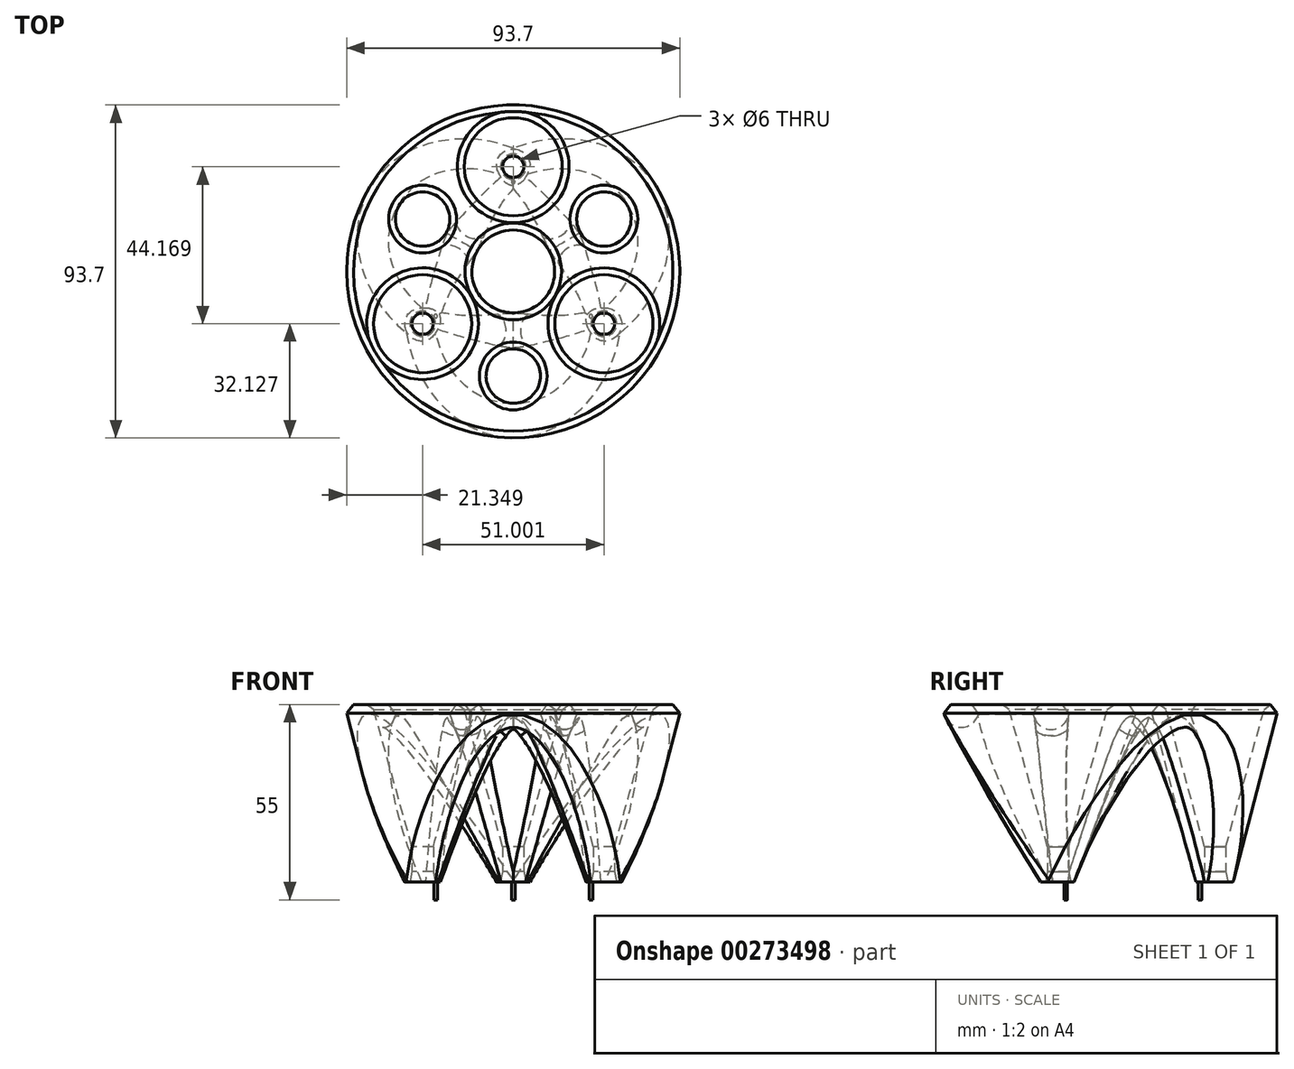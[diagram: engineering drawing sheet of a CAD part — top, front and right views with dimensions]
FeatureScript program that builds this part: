
annotation { "Feature Type Name" : "Feature", "Feature Type Description" : "" }
export const myFeature = defineFeature(function(context is Context, id is Id, definition is map)
    precondition{}
    {
        {
            var Q0;
            Q0=qCreatedBy(makeId("Top.planeOp"),FACE);
            var sketch = newSketch(context, id + "F0", { "sketchPlane" : qUnion([Q0])});
            skCircle(sketch, "E0", {"center": v(0, 0) * mm, "radius": 47.5 * mm});
            skCircle(sketch, "E1", {"center": v(0, 0) * mm, "radius": 11 * mm});
            skCircle(sketch, "E2", {"center": v(0, 29.45) * mm, "radius": 3 * mm});
            skCircle(sketch, "E3.1.0", {"center": v(-25.5, 14.72) * mm, "radius": 3 * mm});
            skCircle(sketch, "E3.2.0", {"center": v(-25.5, -14.72) * mm, "radius": 3 * mm});
            skCircle(sketch, "E4.1.3.0", {"center": v(0, -29.45) * mm, "radius": 3 * mm});
            skCircle(sketch, "E4.1.4.0", {"center": v(25.5, -14.72) * mm, "radius": 3 * mm});
            skCircle(sketch, "E4.1.5.0", {"center": v(25.5, 14.72) * mm, "radius": 3 * mm});
            skCircle(sketch, "E5", {"center": v(0, 25.2) * mm, "radius": 0.5 * mm});
            skCircle(sketch, "E6.1.0", {"center": v(-21.83, -12.6) * mm, "radius": 0.5 * mm});
            skCircle(sketch, "E6.2.0", {"center": v(21.83, -12.6) * mm, "radius": 0.5 * mm});
            skSolve(sketch);
        }
        {
            var Q0;
            Q0=makeQuery(id+"F0.imprint","IMPRINT",FACE,{"disambiguationData":[TD([[makeQuery(id+"F0.imprint","IMPRINT",EDGE,{"derivedFrom":sQuery(id+"F0.wireOp",EDGE,"E0")}),1.0]])]});
            var Q1;
            Q1=makeQuery(id+"F0.imprint","IMPRINT",FACE,{"disambiguationData":[TD([[makeQuery(id+"F0.imprint","IMPRINT",EDGE,{"derivedFrom":sQuery(id+"F0.wireOp",EDGE,"E6.1.0")}),1.0]])]});
            var Q2;
            Q2=makeQuery(id+"F0.imprint","IMPRINT",FACE,{"disambiguationData":[TD([[makeQuery(id+"F0.imprint","IMPRINT",EDGE,{"derivedFrom":sQuery(id+"F0.wireOp",EDGE,"E6.2.0")}),1.0]])]});
            var Q3;
            Q3=makeQuery(id+"F0.imprint","IMPRINT",FACE,{"disambiguationData":[TD([[makeQuery(id+"F0.imprint","IMPRINT",EDGE,{"derivedFrom":sQuery(id+"F0.wireOp",EDGE,"E5")}),1.0]])]});
            extrude(context, id + "F1", {"entities" : qUnion([Q0, Q1, Q2, Q3]), "depth" : 50 * mm});
        }
        {
            var Q0;
            Q0=makeQuery(id+"F0.imprint","IMPRINT",FACE,{"disambiguationData":[TD([[makeQuery(id+"F0.imprint","IMPRINT",EDGE,{"derivedFrom":sQuery(id+"F0.wireOp",EDGE,"E5")}),1.0]])]});
            var Q1;
            Q1=makeQuery(id+"F0.imprint","IMPRINT",FACE,{"disambiguationData":[TD([[makeQuery(id+"F0.imprint","IMPRINT",EDGE,{"derivedFrom":sQuery(id+"F0.wireOp",EDGE,"E6.1.0")}),1.0]])]});
            var Q2;
            Q2=makeQuery(id+"F0.imprint","IMPRINT",FACE,{"disambiguationData":[TD([[makeQuery(id+"F0.imprint","IMPRINT",EDGE,{"derivedFrom":sQuery(id+"F0.wireOp",EDGE,"E6.2.0")}),1.0]])]});
            extrude(context, id + "F2", {"entities" : qUnion([Q0, Q1, Q2]), "operationType" : NewBodyOperationType.ADD, "depth" : 10 * mm, "symmetric" : true});
        }
        {
            var Q0;
            Q0=makeQuery(id+"F1.opExtrude","CAP_EDGE",EDGE,{"disambiguationData":[OSD([sQuery(id+"F0.wireOp",EDGE,"E2")])],"isStart":false});
            var Q1;
            Q1=makeQuery(id+"F1.opExtrude","CAP_EDGE",EDGE,{"disambiguationData":[OSD([sQuery(id+"F0.wireOp",EDGE,"E4.1.4.0")])],"isStart":false});
            var Q2;
            Q2=makeQuery(id+"F1.opExtrude","CAP_EDGE",EDGE,{"disambiguationData":[OSD([sQuery(id+"F0.wireOp",EDGE,"E3.2.0")])],"isStart":false});
            chamfer(context, id + "F3", {"entities" : qUnion([Q0, Q1, Q2]), "chamferType" : ChamferType.TWO_OFFSETS, "width1" : 40 * mm, "oppositeDirection" : false, "width2" : 11.2 * mm, "tangentPropagation" : true});
        }
        {
            var Q0;
            Q0=makeQuery(id+"F1.opExtrude","CAP_EDGE",EDGE,{"disambiguationData":[OSD([sQuery(id+"F0.wireOp",EDGE,"E0")])],"isStart":true});
            chamfer(context, id + "F4", {"entities" : qUnion([Q0]), "chamferType" : ChamferType.TWO_OFFSETS, "width1" : 50 * mm, "oppositeDirection" : false, "width2" : 13 * mm, "tangentPropagation" : true});
        }
        {
            var Q0;
            Q0=makeQuery(id+"F1.opExtrude","CAP_EDGE",EDGE,{"disambiguationData":[OSD([sQuery(id+"F0.wireOp",EDGE,"E2")])],"isStart":true});
            var Q1;
            Q1=makeQuery(id+"F1.opExtrude","CAP_EDGE",EDGE,{"disambiguationData":[OSD([sQuery(id+"F0.wireOp",EDGE,"E3.2.0")])],"isStart":true});
            var Q2;
            Q2=makeQuery(id+"F1.opExtrude","CAP_EDGE",EDGE,{"disambiguationData":[OSD([sQuery(id+"F0.wireOp",EDGE,"E4.1.4.0")])],"isStart":true});
            chamfer(context, id + "F5", {"entities" : qUnion([Q0, Q1, Q2]), "chamferType" : ChamferType.TWO_OFFSETS, "width1" : 0.6 * mm, "oppositeDirection" : false, "width2" : 3 * mm, "tangentPropagation" : true});
        }
        {
            var Q0;
            Q0=makeQuery(id+"F1.opExtrude","CAP_EDGE",EDGE,{"disambiguationData":[OSD([sQuery(id+"F0.wireOp",EDGE,"E1")])],"isStart":true});
            chamfer(context, id + "F6", {"entities" : qUnion([Q0]), "chamferType" : ChamferType.TWO_OFFSETS, "width1" : 13 * mm, "oppositeDirection" : false, "width2" : 50 * mm, "tangentPropagation" : true});
        }
        {
            var Q0;
            Q0=makeQuery(id+"F1.opExtrude","CAP_EDGE",EDGE,{"disambiguationData":[OSD([sQuery(id+"F0.wireOp",EDGE,"E4.1.5.0")])],"isStart":true});
            var Q1;
            Q1=makeQuery(id+"F1.opExtrude","CAP_EDGE",EDGE,{"disambiguationData":[OSD([sQuery(id+"F0.wireOp",EDGE,"E4.1.3.0")])],"isStart":true});
            var Q2;
            Q2=makeQuery(id+"F1.opExtrude","CAP_EDGE",EDGE,{"disambiguationData":[OSD([sQuery(id+"F0.wireOp",EDGE,"E3.1.0")])],"isStart":true});
            chamfer(context, id + "F7", {"entities" : qUnion([Q0, Q1, Q2]), "chamferType" : ChamferType.TWO_OFFSETS, "width1" : 22 * mm, "oppositeDirection" : false, "width2" : 60 * mm, "tangentPropagation" : true});
        }
        {
            var Q0;
            {var subQ0=sQuery(id+"F0.wireOp",EDGE,"E0");Q0=makeQuery(id+"F4.opChamfer","BLEND_EDGE",EDGE,{"blendedFrom":[makeQuery(id+"F1.opExtrude","CAP_EDGE",EDGE,{"disambiguationData":[OSD([subQ0])],"isStart":true}),makeQuery(id+"F1.opExtrude","CAP_FACE",FACE,{"disambiguationData":[OSD([subQ0,sQuery(id+"F0.wireOp",EDGE,"E1"),sQuery(id+"F0.wireOp",EDGE,"E2"),sQuery(id+"F0.wireOp",EDGE,"E3.1.0"),sQuery(id+"F0.wireOp",EDGE,"E3.2.0")])],"isStart":false})],"blendedInto":[makeQuery(id+"F1.opExtrude","CAP_FACE",FACE,{"disambiguationData":[OSD([subQ0,sQuery(id+"F0.wireOp",EDGE,"E1"),sQuery(id+"F0.wireOp",EDGE,"E2"),sQuery(id+"F0.wireOp",EDGE,"E3.1.0"),sQuery(id+"F0.wireOp",EDGE,"E3.2.0")])],"isStart":false})]});}
            var Q1;
            {var subQ0=sQuery(id+"F0.wireOp",EDGE,"E1");Q1=makeQuery(id+"F6.opChamfer","BLEND_EDGE",EDGE,{"blendedFrom":[makeQuery(id+"F1.opExtrude","CAP_EDGE",EDGE,{"disambiguationData":[OSD([subQ0])],"isStart":true}),makeQuery(id+"F1.opExtrude","CAP_FACE",FACE,{"disambiguationData":[OSD([sQuery(id+"F0.wireOp",EDGE,"E0"),subQ0,sQuery(id+"F0.wireOp",EDGE,"E2"),sQuery(id+"F0.wireOp",EDGE,"E3.1.0"),sQuery(id+"F0.wireOp",EDGE,"E3.2.0")])],"isStart":false})],"blendedInto":[makeQuery(id+"F1.opExtrude","CAP_FACE",FACE,{"disambiguationData":[OSD([sQuery(id+"F0.wireOp",EDGE,"E0"),subQ0,sQuery(id+"F0.wireOp",EDGE,"E2"),sQuery(id+"F0.wireOp",EDGE,"E3.1.0"),sQuery(id+"F0.wireOp",EDGE,"E3.2.0")])],"isStart":false})]});}
            var Q2;
            {var subQ0=sQuery(id+"F0.wireOp",EDGE,"E3.2.0");Q2=makeQuery(id+"F3.opChamfer","BLEND_EDGE",EDGE,{"blendedFrom":[makeQuery(id+"F1.opExtrude","CAP_EDGE",EDGE,{"disambiguationData":[OSD([subQ0])],"isStart":false}),makeQuery(id+"F1.opExtrude","CAP_FACE",FACE,{"disambiguationData":[OSD([sQuery(id+"F0.wireOp",EDGE,"E0"),sQuery(id+"F0.wireOp",EDGE,"E1"),sQuery(id+"F0.wireOp",EDGE,"E2"),sQuery(id+"F0.wireOp",EDGE,"E3.1.0"),subQ0,sQuery(id+"F0.wireOp",EDGE,"E4.1.3.0"),sQuery(id+"F0.wireOp",EDGE,"E4.1.4.0"),sQuery(id+"F0.wireOp",EDGE,"E4.1.5.0")])],"isStart":false})],"blendedInto":[makeQuery(id+"F1.opExtrude","CAP_FACE",FACE,{"disambiguationData":[OSD([sQuery(id+"F0.wireOp",EDGE,"E0"),sQuery(id+"F0.wireOp",EDGE,"E1"),sQuery(id+"F0.wireOp",EDGE,"E2"),sQuery(id+"F0.wireOp",EDGE,"E3.1.0"),subQ0,sQuery(id+"F0.wireOp",EDGE,"E4.1.3.0"),sQuery(id+"F0.wireOp",EDGE,"E4.1.4.0"),sQuery(id+"F0.wireOp",EDGE,"E4.1.5.0")])],"isStart":false})]});}
            var Q3;
            {var subQ0=sQuery(id+"F0.wireOp",EDGE,"E2");Q3=makeQuery(id+"F3.opChamfer","BLEND_EDGE",EDGE,{"blendedFrom":[makeQuery(id+"F1.opExtrude","CAP_EDGE",EDGE,{"disambiguationData":[OSD([subQ0])],"isStart":false}),makeQuery(id+"F1.opExtrude","CAP_FACE",FACE,{"disambiguationData":[OSD([sQuery(id+"F0.wireOp",EDGE,"E0"),sQuery(id+"F0.wireOp",EDGE,"E1"),subQ0,sQuery(id+"F0.wireOp",EDGE,"E3.1.0"),sQuery(id+"F0.wireOp",EDGE,"E3.2.0"),sQuery(id+"F0.wireOp",EDGE,"E4.1.3.0"),sQuery(id+"F0.wireOp",EDGE,"E4.1.4.0"),sQuery(id+"F0.wireOp",EDGE,"E4.1.5.0")])],"isStart":false})],"blendedInto":[makeQuery(id+"F1.opExtrude","CAP_FACE",FACE,{"disambiguationData":[OSD([sQuery(id+"F0.wireOp",EDGE,"E0"),sQuery(id+"F0.wireOp",EDGE,"E1"),subQ0,sQuery(id+"F0.wireOp",EDGE,"E3.1.0"),sQuery(id+"F0.wireOp",EDGE,"E3.2.0"),sQuery(id+"F0.wireOp",EDGE,"E4.1.3.0"),sQuery(id+"F0.wireOp",EDGE,"E4.1.4.0"),sQuery(id+"F0.wireOp",EDGE,"E4.1.5.0")])],"isStart":false})]});}
            var Q4;
            {var subQ0=sQuery(id+"F0.wireOp",EDGE,"E4.1.4.0");Q4=makeQuery(id+"F3.opChamfer","BLEND_EDGE",EDGE,{"blendedFrom":[makeQuery(id+"F1.opExtrude","CAP_EDGE",EDGE,{"disambiguationData":[OSD([subQ0])],"isStart":false}),makeQuery(id+"F1.opExtrude","CAP_FACE",FACE,{"disambiguationData":[OSD([sQuery(id+"F0.wireOp",EDGE,"E0"),sQuery(id+"F0.wireOp",EDGE,"E1"),sQuery(id+"F0.wireOp",EDGE,"E2"),sQuery(id+"F0.wireOp",EDGE,"E3.1.0"),sQuery(id+"F0.wireOp",EDGE,"E3.2.0"),sQuery(id+"F0.wireOp",EDGE,"E4.1.3.0"),subQ0,sQuery(id+"F0.wireOp",EDGE,"E4.1.5.0")])],"isStart":false})],"blendedInto":[makeQuery(id+"F1.opExtrude","CAP_FACE",FACE,{"disambiguationData":[OSD([sQuery(id+"F0.wireOp",EDGE,"E0"),sQuery(id+"F0.wireOp",EDGE,"E1"),sQuery(id+"F0.wireOp",EDGE,"E2"),sQuery(id+"F0.wireOp",EDGE,"E3.1.0"),sQuery(id+"F0.wireOp",EDGE,"E3.2.0"),sQuery(id+"F0.wireOp",EDGE,"E4.1.3.0"),subQ0,sQuery(id+"F0.wireOp",EDGE,"E4.1.5.0")])],"isStart":false})]});}
            var Q5;
            Q5=makeQuery(id+"F1.opExtrude","CAP_EDGE",EDGE,{"disambiguationData":[OSD([sQuery(id+"F0.wireOp",EDGE,"E4.1.3.0")])],"isStart":false});
            var Q6;
            Q6=makeQuery(id+"F1.opExtrude","CAP_EDGE",EDGE,{"disambiguationData":[OSD([sQuery(id+"F0.wireOp",EDGE,"E3.1.0")])],"isStart":false});
            var Q7;
            Q7=makeQuery(id+"F1.opExtrude","CAP_EDGE",EDGE,{"disambiguationData":[OSD([sQuery(id+"F0.wireOp",EDGE,"E4.1.5.0")])],"isStart":false});
            var Q8;
            {var subQ0=sQuery(id+"F0.wireOp",EDGE,"E3.1.0");Q8=makeQuery(id+"F7.opChamfer","BLEND_EDGE",EDGE,{"blendedFrom":[makeQuery(id+"F1.opExtrude","CAP_EDGE",EDGE,{"disambiguationData":[OSD([subQ0])],"isStart":true}),makeQuery(id+"F1.opExtrude","CAP_FACE",FACE,{"disambiguationData":[OSD([sQuery(id+"F0.wireOp",EDGE,"E0"),sQuery(id+"F0.wireOp",EDGE,"E1"),sQuery(id+"F0.wireOp",EDGE,"E2"),subQ0,sQuery(id+"F0.wireOp",EDGE,"E3.2.0"),sQuery(id+"F0.wireOp",EDGE,"E4.1.3.0"),sQuery(id+"F0.wireOp",EDGE,"E4.1.4.0"),sQuery(id+"F0.wireOp",EDGE,"E4.1.5.0")])],"isStart":false})],"blendedInto":[makeQuery(id+"F1.opExtrude","CAP_FACE",FACE,{"disambiguationData":[OSD([sQuery(id+"F0.wireOp",EDGE,"E0"),sQuery(id+"F0.wireOp",EDGE,"E1"),sQuery(id+"F0.wireOp",EDGE,"E2"),subQ0,sQuery(id+"F0.wireOp",EDGE,"E3.2.0"),sQuery(id+"F0.wireOp",EDGE,"E4.1.3.0"),sQuery(id+"F0.wireOp",EDGE,"E4.1.4.0"),sQuery(id+"F0.wireOp",EDGE,"E4.1.5.0")])],"isStart":false})]});}
            var Q9;
            {var subQ0=sQuery(id+"F0.wireOp",EDGE,"E4.1.3.0");Q9=makeQuery(id+"F7.opChamfer","BLEND_EDGE",EDGE,{"blendedFrom":[makeQuery(id+"F1.opExtrude","CAP_EDGE",EDGE,{"disambiguationData":[OSD([subQ0])],"isStart":true}),makeQuery(id+"F1.opExtrude","CAP_FACE",FACE,{"disambiguationData":[OSD([sQuery(id+"F0.wireOp",EDGE,"E0"),sQuery(id+"F0.wireOp",EDGE,"E1"),sQuery(id+"F0.wireOp",EDGE,"E2"),sQuery(id+"F0.wireOp",EDGE,"E3.1.0"),sQuery(id+"F0.wireOp",EDGE,"E3.2.0"),subQ0,sQuery(id+"F0.wireOp",EDGE,"E4.1.4.0"),sQuery(id+"F0.wireOp",EDGE,"E4.1.5.0")])],"isStart":false})],"blendedInto":[makeQuery(id+"F1.opExtrude","CAP_FACE",FACE,{"disambiguationData":[OSD([sQuery(id+"F0.wireOp",EDGE,"E0"),sQuery(id+"F0.wireOp",EDGE,"E1"),sQuery(id+"F0.wireOp",EDGE,"E2"),sQuery(id+"F0.wireOp",EDGE,"E3.1.0"),sQuery(id+"F0.wireOp",EDGE,"E3.2.0"),subQ0,sQuery(id+"F0.wireOp",EDGE,"E4.1.4.0"),sQuery(id+"F0.wireOp",EDGE,"E4.1.5.0")])],"isStart":false})]});}
            var Q10;
            {var subQ0=sQuery(id+"F0.wireOp",EDGE,"E4.1.5.0");Q10=makeQuery(id+"F7.opChamfer","BLEND_EDGE",EDGE,{"blendedFrom":[makeQuery(id+"F1.opExtrude","CAP_EDGE",EDGE,{"disambiguationData":[OSD([subQ0])],"isStart":true}),makeQuery(id+"F1.opExtrude","CAP_FACE",FACE,{"disambiguationData":[OSD([sQuery(id+"F0.wireOp",EDGE,"E0"),sQuery(id+"F0.wireOp",EDGE,"E1"),sQuery(id+"F0.wireOp",EDGE,"E2"),sQuery(id+"F0.wireOp",EDGE,"E3.1.0"),sQuery(id+"F0.wireOp",EDGE,"E3.2.0"),sQuery(id+"F0.wireOp",EDGE,"E4.1.3.0"),sQuery(id+"F0.wireOp",EDGE,"E4.1.4.0"),subQ0])],"isStart":false})],"blendedInto":[makeQuery(id+"F1.opExtrude","CAP_FACE",FACE,{"disambiguationData":[OSD([sQuery(id+"F0.wireOp",EDGE,"E0"),sQuery(id+"F0.wireOp",EDGE,"E1"),sQuery(id+"F0.wireOp",EDGE,"E2"),sQuery(id+"F0.wireOp",EDGE,"E3.1.0"),sQuery(id+"F0.wireOp",EDGE,"E3.2.0"),sQuery(id+"F0.wireOp",EDGE,"E4.1.3.0"),sQuery(id+"F0.wireOp",EDGE,"E4.1.4.0"),subQ0])],"isStart":false})]});}
            chamfer(context, id + "F8", {"entities" : qUnion([Q0, Q1, Q2, Q3, Q4, Q5, Q6, Q7, Q8, Q9, Q10]), "width" : 2 * mm, "tangentPropagation" : true});
        }
        {
            var Q0;
            Q0=makeQuery(id+"F7.opChamfer","BLEND_EDGE",EDGE,{"blendedFrom":[makeQuery(id+"F1.opExtrude","CAP_EDGE",EDGE,{"disambiguationData":[OSD([sQuery(id+"F0.wireOp",EDGE,"E4.1.5.0")])],"isStart":true}),makeQuery(id+"F6.opChamfer","BLEND_FACE",FACE,{"disambiguationData":[OSD([sQuery(id+"F0.wireOp",EDGE,"E1")])]})],"blendedInto":[makeQuery(id+"F6.opChamfer","BLEND_FACE",FACE,{"disambiguationData":[OSD([sQuery(id+"F0.wireOp",EDGE,"E1")])]})]});
            var Q1;
            Q1=makeQuery(id+"F7.opChamfer","BLEND_EDGE",EDGE,{"blendedFrom":[makeQuery(id+"F1.opExtrude","CAP_EDGE",EDGE,{"disambiguationData":[OSD([sQuery(id+"F0.wireOp",EDGE,"E3.1.0")])],"isStart":true}),makeQuery(id+"F6.opChamfer","BLEND_FACE",FACE,{"disambiguationData":[OSD([sQuery(id+"F0.wireOp",EDGE,"E1")])]})],"blendedInto":[makeQuery(id+"F6.opChamfer","BLEND_FACE",FACE,{"disambiguationData":[OSD([sQuery(id+"F0.wireOp",EDGE,"E1")])]})]});
            var Q2;
            Q2=makeQuery(id+"F7.opChamfer","BLEND_EDGE",EDGE,{"blendedFrom":[makeQuery(id+"F1.opExtrude","CAP_EDGE",EDGE,{"disambiguationData":[OSD([sQuery(id+"F0.wireOp",EDGE,"E4.1.3.0")])],"isStart":true}),makeQuery(id+"F6.opChamfer","BLEND_FACE",FACE,{"disambiguationData":[OSD([sQuery(id+"F0.wireOp",EDGE,"E1")])]})],"blendedInto":[makeQuery(id+"F6.opChamfer","BLEND_FACE",FACE,{"disambiguationData":[OSD([sQuery(id+"F0.wireOp",EDGE,"E1")])]})]});
            var Q3;
            Q3=makeQuery(id+"F7.opChamfer","BLEND_EDGE",EDGE,{"blendedFrom":[makeQuery(id+"F1.opExtrude","CAP_EDGE",EDGE,{"disambiguationData":[OSD([sQuery(id+"F0.wireOp",EDGE,"E3.1.0")])],"isStart":true}),makeQuery(id+"F4.opChamfer","BLEND_FACE",FACE,{"disambiguationData":[OSD([sQuery(id+"F0.wireOp",EDGE,"E0")])]})],"blendedInto":[makeQuery(id+"F4.opChamfer","BLEND_FACE",FACE,{"disambiguationData":[OSD([sQuery(id+"F0.wireOp",EDGE,"E0")])]})]});
            var Q4;
            Q4=makeQuery(id+"F7.opChamfer","BLEND_EDGE",EDGE,{"blendedFrom":[makeQuery(id+"F1.opExtrude","CAP_EDGE",EDGE,{"disambiguationData":[OSD([sQuery(id+"F0.wireOp",EDGE,"E4.1.5.0")])],"isStart":true}),makeQuery(id+"F4.opChamfer","BLEND_FACE",FACE,{"disambiguationData":[OSD([sQuery(id+"F0.wireOp",EDGE,"E0")])]})],"blendedInto":[makeQuery(id+"F4.opChamfer","BLEND_FACE",FACE,{"disambiguationData":[OSD([sQuery(id+"F0.wireOp",EDGE,"E0")])]})]});
            var Q5;
            Q5=makeQuery(id+"F7.opChamfer","BLEND_EDGE",EDGE,{"blendedFrom":[makeQuery(id+"F1.opExtrude","CAP_EDGE",EDGE,{"disambiguationData":[OSD([sQuery(id+"F0.wireOp",EDGE,"E4.1.3.0")])],"isStart":true}),makeQuery(id+"F4.opChamfer","BLEND_FACE",FACE,{"disambiguationData":[OSD([sQuery(id+"F0.wireOp",EDGE,"E0")])]})],"blendedInto":[makeQuery(id+"F4.opChamfer","BLEND_FACE",FACE,{"disambiguationData":[OSD([sQuery(id+"F0.wireOp",EDGE,"E0")])]})]});
            fillet(context, id + "F9", {"entities" : qUnion([Q0, Q1, Q2, Q3, Q4, Q5]), "radius" : 5 * mm, "tangentPropagation" : true, "allowEdgeOverflow" : false});
        }
    });
